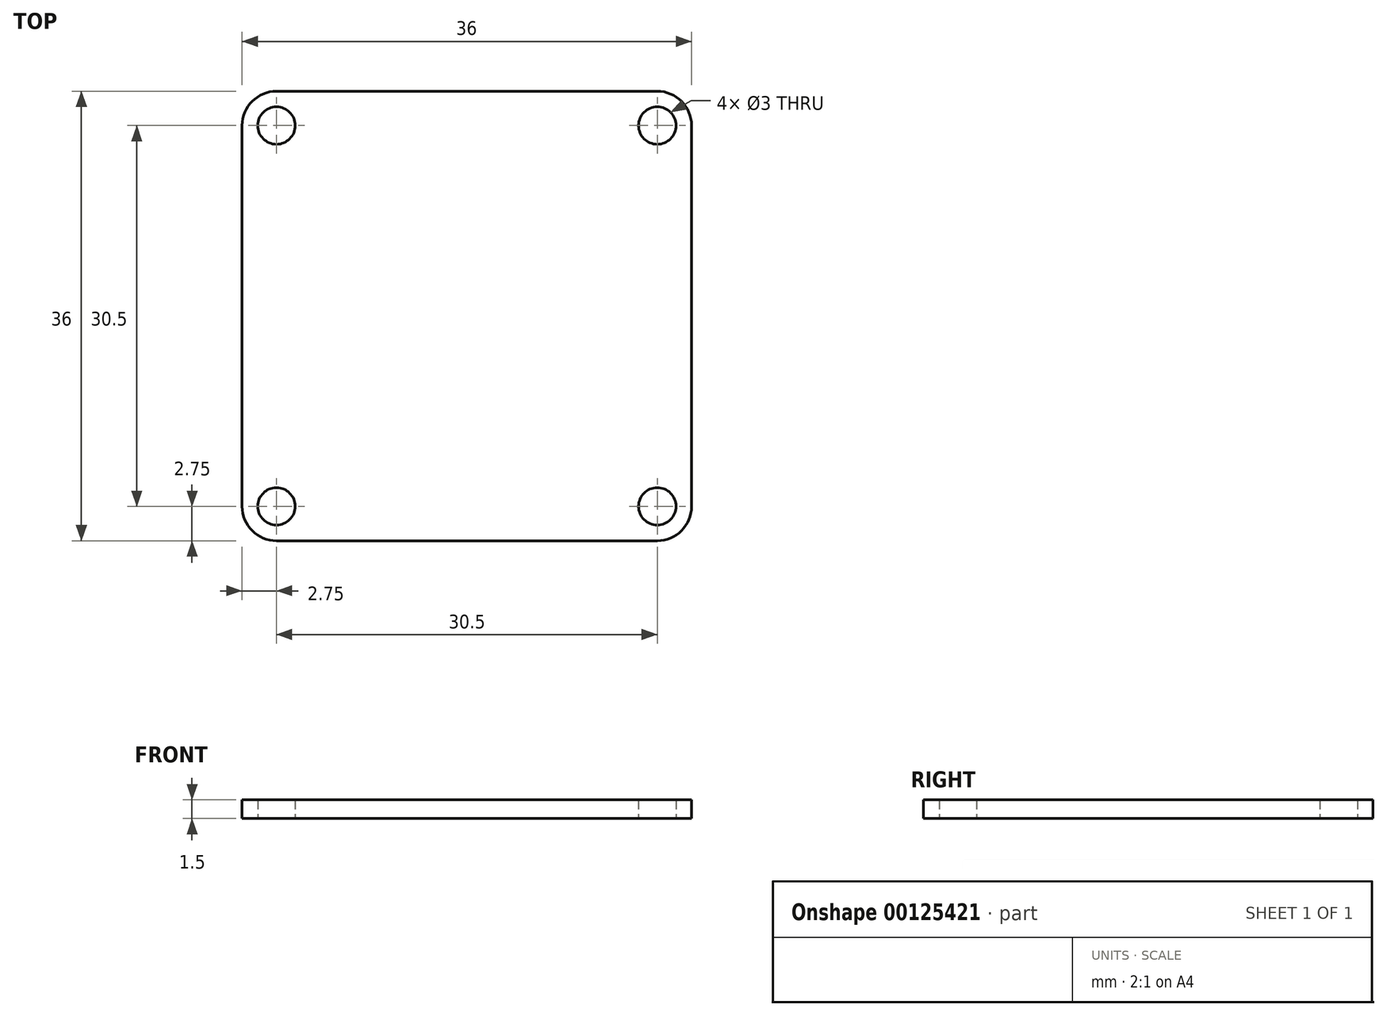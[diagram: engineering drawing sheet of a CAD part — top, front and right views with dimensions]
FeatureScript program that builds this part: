
annotation { "Feature Type Name" : "Feature", "Feature Type Description" : "" }
export const myFeature = defineFeature(function(context is Context, id is Id, definition is map)
    precondition{}
    {
        {
            var Q0;
            Q0=qCreatedBy(makeId("Top.planeOp"),FACE);
            var sketch = newSketch(context, id + "F0", { "sketchPlane" : qUnion([Q0])});
            skCircle(sketch, "E0", {"center": v(-15.25, 15.25) * mm, "radius": 1.5 * mm});
            skCircle(sketch, "E1.0.1.0", {"center": v(-15.25, -15.25) * mm, "radius": 1.5 * mm});
            skCircle(sketch, "E1.1.0.0", {"center": v(15.25, 15.25) * mm, "radius": 1.5 * mm});
            skCircle(sketch, "E1.1.1.0", {"center": v(15.25, -15.25) * mm, "radius": 1.5 * mm});
            skLineSegment(sketch, "E1.direction1", {"start": v(-15.25, 15.25) * mm, "end": v(15.25, 15.25) * mm, "construction": true});
            skLineSegment(sketch, "E1.direction2", {"start": v(-15.25, 15.25) * mm, "end": v(-15.25, -15.25) * mm, "construction": true});
            skLineSegment(sketch, "E2.bottom", {"start": v(-15.25, 18) * mm, "end": v(15.25, 18) * mm});
            skLineSegment(sketch, "E2.top", {"start": v(-15.25, -18) * mm, "end": v(15.25, -18) * mm});
            skLineSegment(sketch, "E2.left", {"start": v(-18, 15.25) * mm, "end": v(-18, -15.25) * mm});
            skLineSegment(sketch, "E2.right", {"start": v(18, 15.25) * mm, "end": v(18, -15.25) * mm});
            skArc(sketch, "E3", {"start": v(-15.25, 18) * mm, "mid": v(-17.2, 17.2) * mm, "end": v(-18, 15.25) * mm});
            skArc(sketch, "E4", {"start": v(-18, -15.25) * mm, "mid": v(-17.2, -17.2) * mm, "end": v(-15.25, -18) * mm});
            skArc(sketch, "E5", {"start": v(15.25, -18) * mm, "mid": v(17.2, -17.2) * mm, "end": v(18, -15.25) * mm});
            skArc(sketch, "E6", {"start": v(18, 15.25) * mm, "mid": v(17.2, 17.2) * mm, "end": v(15.25, 18) * mm});
            skSolve(sketch);
        }
        {
            var Q0;
            Q0 = qSketchRegion(id + "F0", true);
            extrude(context, id + "F1", {"entities" : qUnion([Q0]), "depth" : 1.5 * mm});
        }
    });
